# Revit family: svetilnik_supremus_mini
name_source: partatom
category: Осветительные приборы
revit_build: Autodesk Revit 2016 (Build: 20150506_1715(x64)
units: mm (PartAtom-declared; Revit-internal decimal feet)

## family parameters
Всегда вертикально = Да
Источник света = Нет
На основе рабочей плоскости = Нет
Общий = Нет
При загрузке вырезать с полостями = Нет
Размер круглого соединителя = Использовать диаметр
Тип детали = Нормальный
Точка расчета площади = Нет

## types (1)
- Супремус-мини
    ADSK_Артикул = ДТУ441
    ADSK_Единица измерения = шт.
    ADSK_Завод-изготовитель = ALFRESCO
    ADSK_Количество фаз = 2
    ADSK_Количество фаз числовое = 2
    ADSK_Коэффициент мощности = 0.98
    ADSK_Масса = 3.1
    ADSK_Модель = ДТУ-44-AF Супремус-мини
    ADSK_Наименование = Светодиодный светильник Супремус-мини ДТУ-44-AF-6Вт-0,75
    ADSK_Напряжение = 220 В
    ADSK_Номинальная мощность = 6 Вт
    ADSK_Полная мощность = 6 В·А
    ADSK_Размер_Высота = 750 мм
    ADSK_Размер_Длина = 190 мм
    ADSK_Размер_Ширина = 190 мм
    ADSK_Ток = 0 А
    ADSK_Энергоэффективность = 100 лм/Вт
    IP Class = IP 65
    URL = http://www.allfresco.ru
    Блок аварийного питания = Нет
    Высота крышки = 85 мм
    Высота плафона = 100 мм
    Изготовитель = ALFRESCO
    Класс защиты = 1
    Класс пожароопасности = F (светильники предназначены для установки непосредственно на поверхность из нормально воспламеняемых материалов)
    Климатическая зона = У1
    Корпус светильника = Сталь крашенная чёрная
    Материал рассеивателя = Прозрачное закаленное стекло
    Область использования = ландшафт, коттедж. Посёлки,микрорайоны
    Плафон = Прозрачное закаленное стекло
    Полная установленная мощность = 6 В·А
    Световой поток 2 = 600 лм
    Температура эксплуатации = -35 +40
    Тип ИС = LED-светодиоды
    Тип КСС = Концентрированная
    Тип ПРА = -
    Тип продукции = LED-светильник
    Цветовая температура = 2700-6500

## geometry (parser evidence)
native form markers: Blend x2
no freeform markers — native parametric forms only
